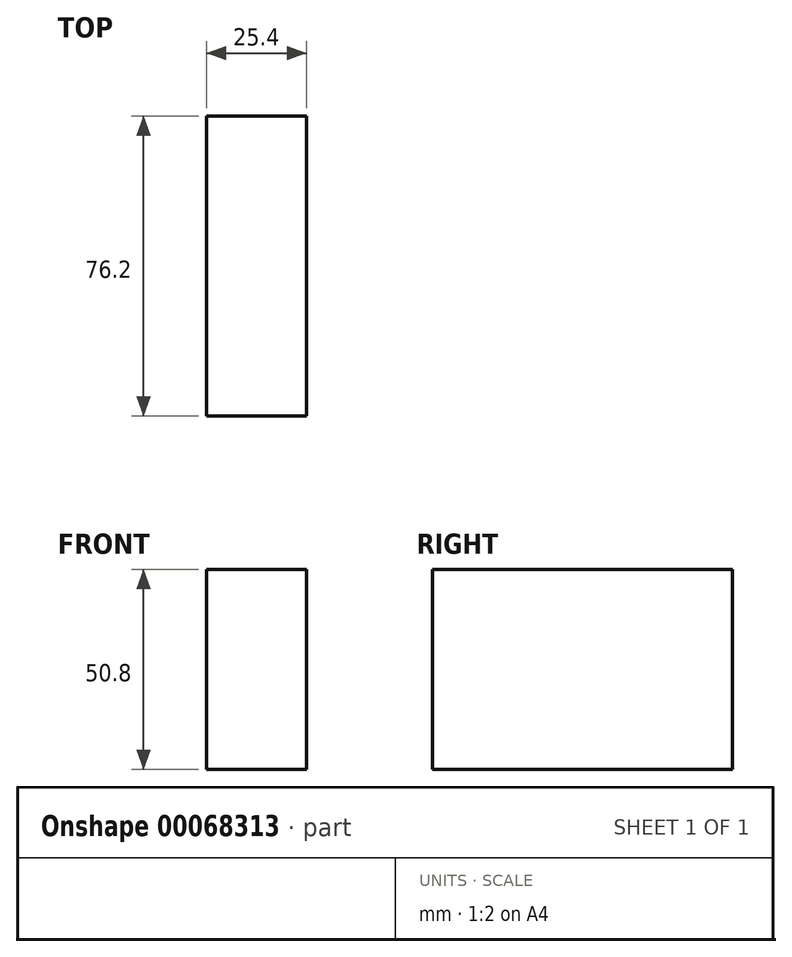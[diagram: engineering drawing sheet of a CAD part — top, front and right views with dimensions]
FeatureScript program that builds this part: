
annotation { "Feature Type Name" : "Feature", "Feature Type Description" : "" }
export const myFeature = defineFeature(function(context is Context, id is Id, definition is map)
    precondition{}
    {
        {
            var Q0;
            Q0=qCreatedBy(makeId("Front.planeOp"),FACE);
            var sketch = newSketch(context, id + "F0", { "sketchPlane" : qUnion([Q0])});
            skLineSegment(sketch, "E0", {"start": v(0, 0) * mm, "end": v(25.4, 0) * mm});
            skLineSegment(sketch, "E1", {"start": v(25.4, 0) * mm, "end": v(25.4, 50.8) * mm});
            skLineSegment(sketch, "E2", {"start": v(25.4, 50.8) * mm, "end": v(0, 50.8) * mm});
            skLineSegment(sketch, "E3", {"start": v(0, 50.8) * mm, "end": v(0, 0) * mm});
            skSolve(sketch);
        }
        {
            var Q0;
            Q0=makeQuery(id+"F0.imprint","IMPRINT",FACE,{"disambiguationData":[TD([[makeQuery(id+"F0.imprint","IMPRINT",EDGE,{"derivedFrom":sQuery(id+"F0.wireOp",EDGE,"E0")}),1.0]])]});
            extrude(context, id + "F1", {"entities" : qUnion([Q0]), "depth" : 76.2 * mm});
        }
    });
